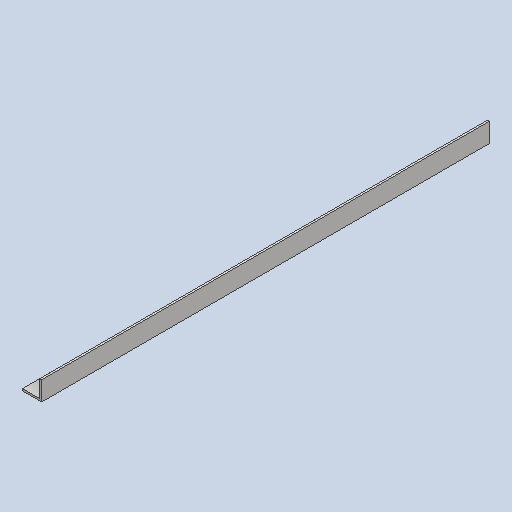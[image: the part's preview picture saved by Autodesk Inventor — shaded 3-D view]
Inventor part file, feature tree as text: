
AUTODESK INVENTOR PART (.ipt)
format: ipt  version: 2023 (Build 270158000, 158)  size: 84,480 bytes
history: native  units: mm
features: extrude x1, sketch x1
ambient origin geometry x8: Origin, YZ Plane, XZ Plane, XY Plane, X Axis, Y Axis, Z Axis, Center Point
bodies: Solid1 (feature_tree)
feature tree (2):
  extrude  "Extrusion1"  Depth=20.0mm
  sketch  "Sketch1"  dims[d0=20.0mm d1=20.0mm d2=2.0mm d3=2.0mm d4=465.0mm d5=0.0mm]
